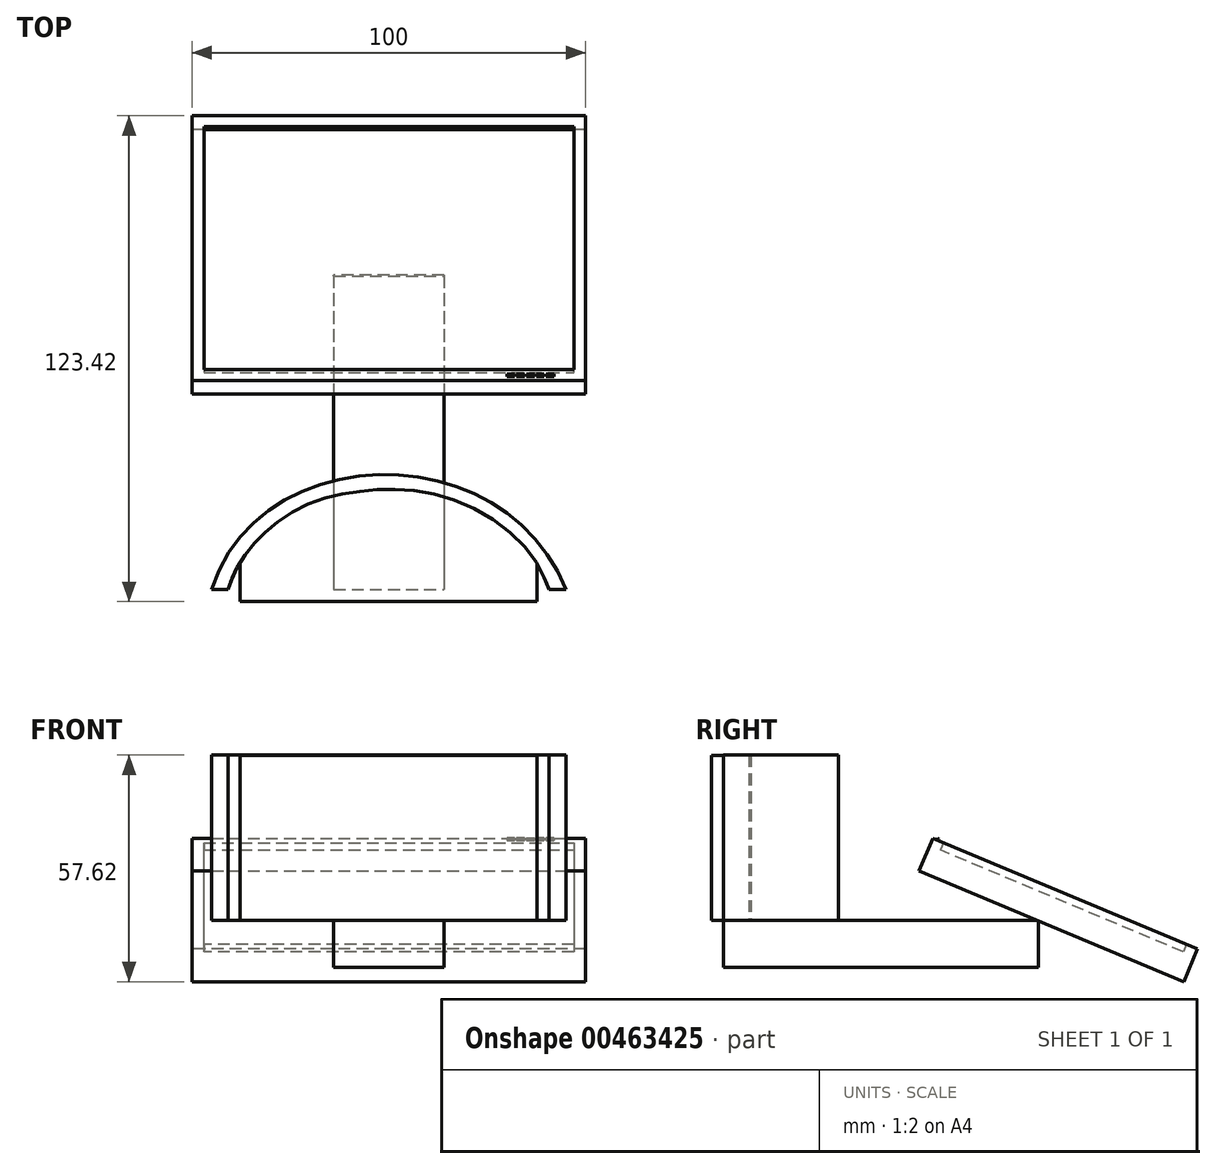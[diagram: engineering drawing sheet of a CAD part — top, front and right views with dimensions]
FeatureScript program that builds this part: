
annotation { "Feature Type Name" : "Feature", "Feature Type Description" : "" }
export const myFeature = defineFeature(function(context is Context, id is Id, definition is map)
    precondition{}
    {
        {
            var Q0;
            Q0=qCreatedBy(makeId("Top.planeOp"),FACE);
            var sketch = newSketch(context, id + "F0", { "sketchPlane" : qUnion([Q0])});
            skFitSpline(sketch, "E0", {"points": [v(45, 0) * mm, v(0, 29.24) * mm, v(-45, 0) * mm], "startDerivative": vector(-44.06, 112.3) * mm, "endDerivative": vector(-34.98, -118.52) * mm});
            skFitSpline(sketch, "E1.0", {"points": [v(41.28, -1.46) * mm, v(39.6, 2.8) * mm, v(35.02, 10.33) * mm, v(25.2, 18.66) * mm, v(13.22, 23.9) * mm, v(2.2, 25.5) * mm, v(-6.76, 25.04) * mm, v(-15.58, 23.42) * mm, v(-23.82, 20.08) * mm, v(-30.8, 15.1) * mm, v(-35.25, 10.55) * mm, v(-38.81, 5.2) * mm, v(-40.5, 1.08) * mm, v(-41.16, -1.13) * mm]});
            skLineSegment(sketch, "E2", {"start": v(-45, 0) * mm, "end": v(-40.8, 0) * mm});
            skLineSegment(sketch, "E3", {"start": v(45, 0) * mm, "end": v(40.67, 0) * mm});
            skSolve(sketch);
        }
        {
            var Q0;
            Q0=makeQuery(id+"F0.imprint","IMPRINT",FACE,{"disambiguationData":[TD([[makeQuery(id+"F0.imprint","IMPRINT",EDGE,{"derivedFrom":sQuery(id+"F0.wireOp",EDGE,"E0")}),1.0]])]});
            extrude(context, id + "F1", {"entities" : qUnion([Q0]), "depth" : 42 * mm});
        }
        {
            var Q0;
            Q0=qCreatedBy(makeId("Front.planeOp"),FACE);
            var sketch = newSketch(context, id + "F2", { "sketchPlane" : qUnion([Q0])});
            skLineSegment(sketch, "E4.bottom", {"start": v(37.67, 0) * mm, "end": v(-37.8, 0) * mm});
            skLineSegment(sketch, "E4.top", {"start": v(37.67, 41.91) * mm, "end": v(-37.8, 41.91) * mm});
            skLineSegment(sketch, "E4.left", {"start": v(37.67, 0) * mm, "end": v(37.67, 41.91) * mm});
            skLineSegment(sketch, "E4.right", {"start": v(-37.8, 0) * mm, "end": v(-37.8, 41.91) * mm});
            skSolve(sketch);
        }
        {
            var Q0;
            Q0 = qSketchRegion(id + "F2", true);
            var Q1;
            Q1=makeQuery(id+"F1.opExtrude","SWEPT_BODY",BODY,{"disambiguationData":[OSD([sQuery(id+"F0.wireOp",EDGE,"E0"),sQuery(id+"F0.wireOp",EDGE,"E1.0"),sQuery(id+"F0.wireOp",EDGE,"E2"),sQuery(id+"F0.wireOp",EDGE,"E3")])]});
            extrude(context, id + "F3", {"entities" : qUnion([Q0]), "operationType" : NewBodyOperationType.ADD, "endBound" : BoundingType.UP_TO_BODY, "oppositeDirection" : true, "endBoundEntityBody" : qUnion([Q1]), "depth" : 25 * mm});
        }
        {
            var Q0;
            Q0=makeQuery(id+"F3.opExtrude","CAP_FACE",FACE,{"disambiguationData":[OSD([sQuery(id+"F2.wireOp",EDGE,"E4.bottom"),sQuery(id+"F2.wireOp",EDGE,"E4.top"),sQuery(id+"F2.wireOp",EDGE,"E4.left"),sQuery(id+"F2.wireOp",EDGE,"E4.right")])],"isStart":true});
            var sketch = newSketch(context, id + "F4", { "sketchPlane" : qUnion([Q0])});
            skLineSegment(sketch, "E5.bottom", {"start": v(-37.8, 41.91) * mm, "end": v(37.67, 41.91) * mm});
            skLineSegment(sketch, "E5.top", {"start": v(-37.8, 0) * mm, "end": v(37.67, 0) * mm});
            skLineSegment(sketch, "E5.left", {"start": v(-37.8, 41.91) * mm, "end": v(-37.8, 0) * mm});
            skLineSegment(sketch, "E5.right", {"start": v(37.67, 41.91) * mm, "end": v(37.67, 0) * mm});
            skSolve(sketch);
        }
        {
            var Q0;
            Q0=makeQuery(id+"F4.imprint","IMPRINT",FACE,{"disambiguationData":[TD([[makeQuery(id+"F4.imprint","IMPRINT",EDGE,{"derivedFrom":sQuery(id+"F4.wireOp",EDGE,"E5.bottom")}),1.0]])]});
            extrude(context, id + "F5", {"entities" : qUnion([Q0]), "operationType" : NewBodyOperationType.ADD, "depth" : 3 * mm});
        }
        {
            var Q0;
            Q0=qCreatedBy(makeId("Front.planeOp"),FACE);
            var sketch = newSketch(context, id + "F6", { "sketchPlane" : qUnion([Q0])});
            skLineSegment(sketch, "E6.bottom", {"start": v(-14, 0) * mm, "end": v(14, 0) * mm});
            skLineSegment(sketch, "E6.top", {"start": v(-14, -12) * mm, "end": v(14, -12) * mm});
            skLineSegment(sketch, "E6.left", {"start": v(-14, 0) * mm, "end": v(-14, -12) * mm});
            skLineSegment(sketch, "E6.right", {"start": v(14, 0) * mm, "end": v(14, -12) * mm});
            skPoint(sketch, "E7", {"position": v(0, -12) * mm});
            skSolve(sketch);
        }
        {
            var Q0;
            Q0=qCreatedBy(makeId("Front.planeOp"),FACE);
            var sketch = newSketch(context, id + "F7", { "sketchPlane" : qUnion([Q0])});
            skLineSegment(sketch, "E8.bottom", {"start": v(13.5, 0) * mm, "end": v(-13.5, 0) * mm});
            skLineSegment(sketch, "E8.top", {"start": v(13.5, -11.5) * mm, "end": v(-13.5, -11.5) * mm});
            skLineSegment(sketch, "E8.left", {"start": v(13.5, 0) * mm, "end": v(13.5, -11.5) * mm});
            skLineSegment(sketch, "E8.right", {"start": v(-13.5, 0) * mm, "end": v(-13.5, -11.5) * mm});
            skSolve(sketch);
        }
        {
            var Q0;
            Q0=makeQuery(id+"F6.imprint","IMPRINT",FACE,{"disambiguationData":[TD([[makeQuery(id+"F6.imprint","IMPRINT",EDGE,{"derivedFrom":sQuery(id+"F6.wireOp",EDGE,"E6.bottom")}),-1.0]])]});
            extrude(context, id + "F8", {"entities" : qUnion([Q0]), "operationType" : NewBodyOperationType.ADD, "oppositeDirection" : true, "depth" : 80 * mm});
        }
        {
            var Q0;
            Q0=qCreatedBy(makeId("Right.planeOp"),FACE);
            var sketch = newSketch(context, id + "F9", { "sketchPlane" : qUnion([Q0])});
            skLineSegment(sketch, "E9", {"start": v(102.12, -9.4) * mm, "end": v(53.4, 11) * mm});
            skSolve(sketch);
        }
        {
            var Q0;
            Q0=sQuery(id+"F9.wireOp",EDGE,"E9");
            var Q1;
            Q1=qCreatedBy(makeId("Front.planeOp"),FACE);
            cPlane(context, id + "F10", {"entities" : qUnion([Q0, Q1]), "cplaneType" : CPlaneType.LINE_ANGLE, "offset" : 25 * mm, "angle" : 0 * degree, "width" : 150 * mm, "height" : 150 * mm});
        }
        {
            var Q0;
            Q0=qCreatedBy(id+"F10.planeOp",FACE);
            var sketch = newSketch(context, id + "F11", { "sketchPlane" : qUnion([Q0])});
            skLineSegment(sketch, "E10", {"start": v(-50, 113.9) * mm, "end": v(-50, 41) * mm});
            skLineSegment(sketch, "E11", {"start": v(-50, 41) * mm, "end": v(50, 41) * mm});
            skLineSegment(sketch, "E12", {"start": v(50, 41) * mm, "end": v(50, 113.9) * mm});
            skLineSegment(sketch, "E13", {"start": v(50, 113.9) * mm, "end": v(-50, 113.9) * mm});
            skSolve(sketch);
        }
        {
            var Q0;
            Q0=makeQuery(id+"F11.imprint","IMPRINT",FACE,{"disambiguationData":[TD([[makeQuery(id+"F11.imprint","IMPRINT",EDGE,{"derivedFrom":sQuery(id+"F11.wireOp",EDGE,"E10")}),1.0]])]});
            extrude(context, id + "F12", {"entities" : qUnion([Q0]), "operationType" : NewBodyOperationType.ADD, "depth" : 7 * mm});
        }
        {
            var Q0;
            Q0=makeQuery(id+"F12.opExtrude","CAP_FACE",FACE,{"disambiguationData":[OSD([sQuery(id+"F11.wireOp",EDGE,"E10"),sQuery(id+"F11.wireOp",EDGE,"E11"),sQuery(id+"F11.wireOp",EDGE,"E12"),sQuery(id+"F11.wireOp",EDGE,"E13")])],"isStart":false});
            var sketch = newSketch(context, id + "F13", { "sketchPlane" : qUnion([Q0])});
            skLineSegment(sketch, "E14", {"start": v(-47, 110.9) * mm, "end": v(-47, 44) * mm});
            skLineSegment(sketch, "E15", {"start": v(-47, 44) * mm, "end": v(47, 44) * mm});
            skLineSegment(sketch, "E16", {"start": v(47, 44) * mm, "end": v(47, 110.9) * mm});
            skLineSegment(sketch, "E17", {"start": v(47, 110.9) * mm, "end": v(-47, 110.9) * mm});
            skLineSegment(sketch, "E18", {"start": v(-50, 113.9) * mm, "end": v(-50, 41) * mm});
            skLineSegment(sketch, "E19", {"start": v(-50, 41) * mm, "end": v(50, 41) * mm});
            skLineSegment(sketch, "E20", {"start": v(50, 41) * mm, "end": v(50, 113.9) * mm});
            skLineSegment(sketch, "E21", {"start": v(50, 113.9) * mm, "end": v(-50, 113.9) * mm});
            skSolve(sketch);
        }
        {
            var Q0;
            Q0=makeQuery(id+"F13.imprint","IMPRINT",FACE,{"disambiguationData":[TD([[makeQuery(id+"F13.imprint","IMPRINT",EDGE,{"derivedFrom":sQuery(id+"F13.wireOp",EDGE,"E14")}),-1.0]])]});
            extrude(context, id + "F14", {"entities" : qUnion([Q0]), "operationType" : NewBodyOperationType.ADD, "depth" : 2 * mm});
        }
        {
            var Q0;
            Q0=makeQuery(id+"F14.opExtrude","CAP_FACE",FACE,{"disambiguationData":[OSD([sQuery(id+"F13.wireOp",EDGE,"E14"),sQuery(id+"F13.wireOp",EDGE,"E15"),sQuery(id+"F13.wireOp",EDGE,"E16"),sQuery(id+"F13.wireOp",EDGE,"E17"),sQuery(id+"F13.wireOp",EDGE,"E18"),sQuery(id+"F13.wireOp",EDGE,"E19"),sQuery(id+"F13.wireOp",EDGE,"E20"),sQuery(id+"F13.wireOp",EDGE,"E21")])],"isStart":false});
            var sketch = newSketch(context, id + "F15", { "sketchPlane" : qUnion([Q0])});
            skLineSegment(sketch, "E22", {"start": v(41.97, 42.06) * mm, "end": v(39.97, 42.06) * mm});
            skLineSegment(sketch, "E23", {"start": v(32.47, 42.06) * mm, "end": v(32.47, 42.56) * mm});
            skLineSegment(sketch, "E24", {"start": v(32.47, 42.56) * mm, "end": v(34.47, 42.56) * mm});
            skLineSegment(sketch, "E25", {"start": v(34.47, 42.56) * mm, "end": v(34.47, 42.06) * mm});
            skLineSegment(sketch, "E26", {"start": v(34.97, 42.56) * mm, "end": v(34.97, 42.06) * mm});
            skLineSegment(sketch, "E27", {"start": v(34.97, 42.06) * mm, "end": v(36.97, 42.06) * mm});
            skLineSegment(sketch, "E28", {"start": v(36.97, 42.06) * mm, "end": v(36.97, 42.56) * mm});
            skLineSegment(sketch, "E29.trimOffspring", {"start": v(34.47, 42.06) * mm, "end": v(32.47, 42.06) * mm});
            skLineSegment(sketch, "E30.trimOffspring", {"start": v(34.97, 42.56) * mm, "end": v(36.97, 42.56) * mm});
            skLineSegment(sketch, "E31", {"start": v(37.47, 42.56) * mm, "end": v(37.47, 42.06) * mm});
            skLineSegment(sketch, "E32", {"start": v(39.47, 42.56) * mm, "end": v(39.47, 42.06) * mm});
            skLineSegment(sketch, "E33.trimOffspring", {"start": v(37.47, 42.56) * mm, "end": v(39.47, 42.56) * mm});
            skLineSegment(sketch, "E34.trimOffspring", {"start": v(36.97, 42.06) * mm, "end": v(34.97, 42.06) * mm});
            skLineSegment(sketch, "E35", {"start": v(39.97, 42.56) * mm, "end": v(39.97, 42.06) * mm});
            skLineSegment(sketch, "E36", {"start": v(39.97, 42.06) * mm, "end": v(41.97, 42.06) * mm});
            skLineSegment(sketch, "E37", {"start": v(41.97, 42.06) * mm, "end": v(41.97, 42.56) * mm});
            skLineSegment(sketch, "E38.trimOffspring", {"start": v(39.97, 42.56) * mm, "end": v(41.97, 42.56) * mm});
            skLineSegment(sketch, "E39.trimOffspring", {"start": v(39.47, 42.06) * mm, "end": v(37.47, 42.06) * mm});
            skLineSegment(sketch, "E40", {"start": v(31.97, 42.56) * mm, "end": v(31.97, 42.06) * mm});
            skLineSegment(sketch, "E41", {"start": v(31.97, 42.06) * mm, "end": v(29.97, 42.06) * mm});
            skLineSegment(sketch, "E42", {"start": v(29.97, 42.06) * mm, "end": v(29.97, 42.56) * mm});
            skLineSegment(sketch, "E43", {"start": v(29.97, 42.56) * mm, "end": v(31.97, 42.56) * mm});
            skSolve(sketch);
        }
        {
            var Q0;
            Q0=makeQuery(id+"F15.imprint","IMPRINT",FACE,{"disambiguationData":[TD([[makeQuery(id+"F15.imprint","IMPRINT",EDGE,{"derivedFrom":sQuery(id+"F15.wireOp",EDGE,"E23")}),-1.0]])]});
            var Q1;
            Q1=makeQuery(id+"F15.imprint","IMPRINT",FACE,{"disambiguationData":[TD([[makeQuery(id+"F15.imprint","IMPRINT",EDGE,{"derivedFrom":sQuery(id+"F15.wireOp",EDGE,"E26")}),1.0]])]});
            var Q2;
            Q2=makeQuery(id+"F15.imprint","IMPRINT",FACE,{"disambiguationData":[TD([[makeQuery(id+"F15.imprint","IMPRINT",EDGE,{"derivedFrom":sQuery(id+"F15.wireOp",EDGE,"E31")}),1.0]])]});
            var Q3;
            Q3=makeQuery(id+"F15.imprint","IMPRINT",FACE,{"disambiguationData":[TD([[makeQuery(id+"F15.imprint","IMPRINT",EDGE,{"derivedFrom":sQuery(id+"F15.wireOp",EDGE,"E35")}),1.0]])]});
            var Q4;
            Q4=makeQuery(id+"F15.imprint","IMPRINT",FACE,{"disambiguationData":[TD([[makeQuery(id+"F15.imprint","IMPRINT",EDGE,{"derivedFrom":sQuery(id+"F15.wireOp",EDGE,"E40")}),-1.0]])]});
            extrude(context, id + "F16", {"entities" : qUnion([Q0, Q1, Q2, Q3, Q4]), "operationType" : NewBodyOperationType.ADD, "depth" : 0.5 * mm});
        }
    });
